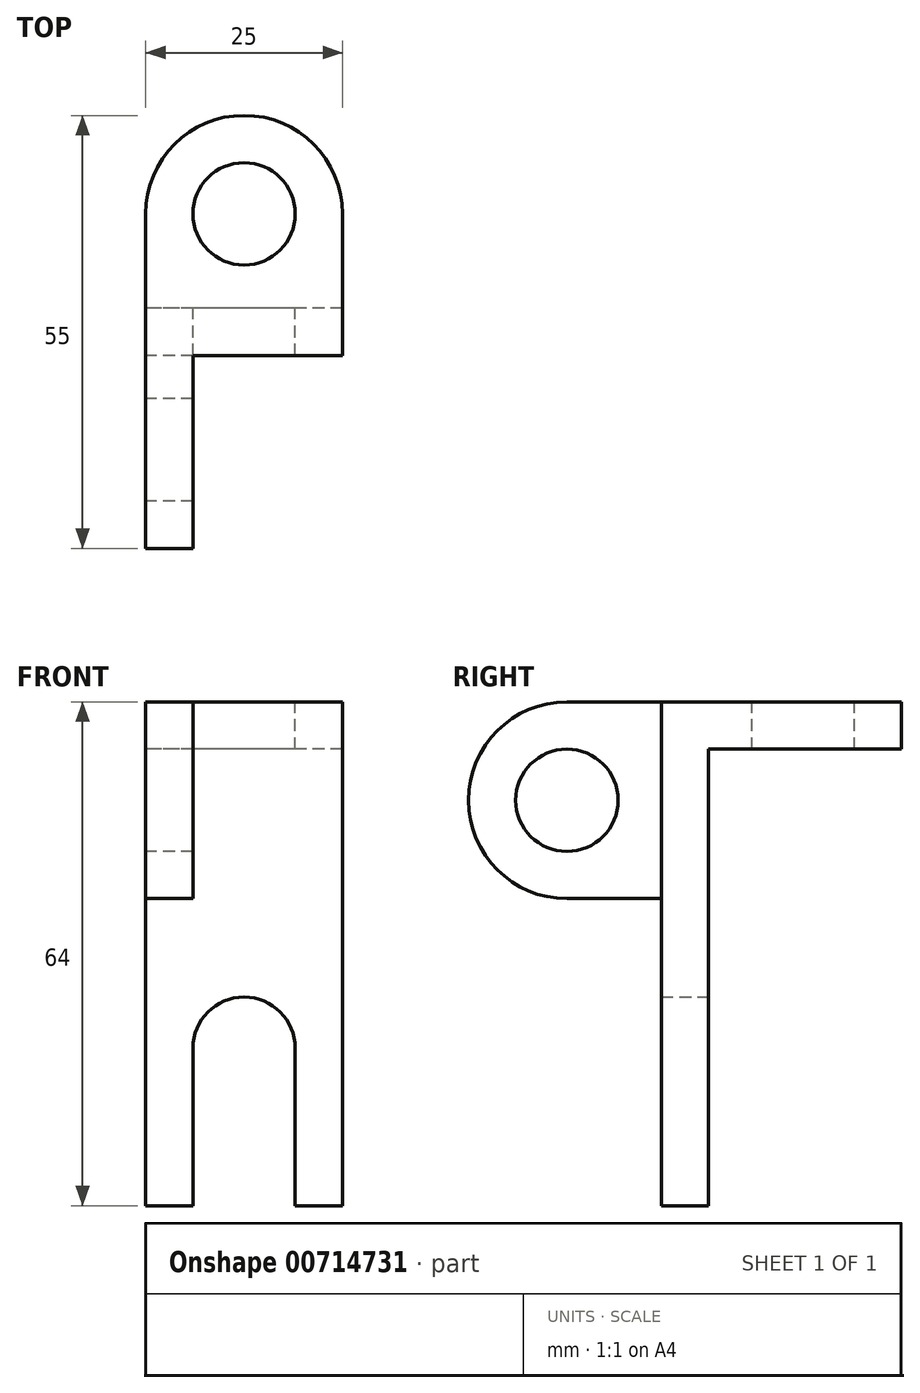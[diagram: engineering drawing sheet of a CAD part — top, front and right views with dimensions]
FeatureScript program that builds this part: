
annotation { "Feature Type Name" : "Feature", "Feature Type Description" : "" }
export const myFeature = defineFeature(function(context is Context, id is Id, definition is map)
    precondition{}
    {
        {
            var Q0;
            Q0=qCreatedBy(makeId("Front.planeOp"),FACE);
            var sketch = newSketch(context, id + "F0", { "sketchPlane" : qUnion([Q0])});
            skLineSegment(sketch, "E0.bottom", {"start": v(12.5, 32) * mm, "end": v(-12.5, 32) * mm});
            skLineSegment(sketch, "E0.top", {"start": v(12.5, -32) * mm, "end": v(-12.5, -32) * mm});
            skLineSegment(sketch, "E0.left", {"start": v(12.5, 32) * mm, "end": v(12.5, -32) * mm});
            skLineSegment(sketch, "E0.right", {"start": v(-12.5, 32) * mm, "end": v(-12.5, -32) * mm});
            skPoint(sketch, "E0.middle", {"position": v(0, 0) * mm});
            skLineSegment(sketch, "E1.bottom", {"start": v(6.5, -32) * mm, "end": v(-6.5, -32) * mm});
            skLineSegment(sketch, "E1.top", {"start": v(6.5, -12) * mm, "end": v(-6.5, -12) * mm});
            skLineSegment(sketch, "E1.left", {"start": v(6.5, -32) * mm, "end": v(6.5, -12) * mm});
            skLineSegment(sketch, "E1.right", {"start": v(-6.5, -32) * mm, "end": v(-6.5, -12) * mm});
            skPoint(sketch, "E1.middle", {"position": v(0, -22) * mm});
            skCircle(sketch, "E2", {"center": v(0, -12) * mm, "radius": 6.5 * mm});
            skSolve(sketch);
        }
        {
            var Q0;
            Q0=makeQuery(id+"F0.imprint","IMPRINT",FACE,{"disambiguationData":[TD([[makeQuery(id+"F0.imprint","IMPRINT",EDGE,{"derivedFrom":sQuery(id+"F0.wireOp",EDGE,"E0.bottom")}),1.0]])]});
            extrude(context, id + "F1", {"entities" : qUnion([Q0]), "depth" : 6 * mm, "offsetDistance" : 25 * mm});
        }
        {
            var Q0;
            Q0=makeQuery(id+"F1.opExtrude","SWEPT_FACE",FACE,{"disambiguationData":[OSD([sQuery(id+"F0.wireOp",EDGE,"E0.bottom")])]});
            var sketch = newSketch(context, id + "F2", { "sketchPlane" : qUnion([Q0])});
            skLineSegment(sketch, "E3.bottom", {"start": v(12.5, -6) * mm, "end": v(-12.5, -6) * mm});
            skLineSegment(sketch, "E3.top", {"start": v(12.5, 12) * mm, "end": v(6.5, 12) * mm, "construction": true});
            skLineSegment(sketch, "E3.left", {"start": v(12.5, -6) * mm, "end": v(12.5, 12) * mm});
            skLineSegment(sketch, "E3.right", {"start": v(-12.5, -6) * mm, "end": v(-12.5, 12) * mm});
            skCircle(sketch, "E4", {"center": v(0, 12) * mm, "radius": 12.5 * mm});
            skCircle(sketch, "E5", {"center": v(0, 12) * mm, "radius": 6.5 * mm});
            skLineSegment(sketch, "E6.trimOffspring", {"start": v(-6.5, 12) * mm, "end": v(-12.5, 12) * mm, "construction": true});
            skSolve(sketch);
        }
        {
            var Q0;
            Q0=qSketchRegion(id+"F2",true);
            extrude(context, id + "F3", {"entities" : qUnion([Q0]), "operationType" : NewBodyOperationType.ADD, "oppositeDirection" : true, "depth" : 6 * mm, "offsetDistance" : 25 * mm});
        }
        {
            var Q0;
            Q0=makeQuery(id+"F3.boolean.opBoolean","MERGE",FACE,{"derivedFrom":[makeQuery(id+"F1.opExtrude","SWEPT_FACE",FACE,{"disambiguationData":[OSD([sQuery(id+"F0.wireOp",EDGE,"E0.right")])]}),makeQuery(id+"F3.opExtrude","SWEPT_FACE",FACE,{"disambiguationData":[OSD([sQuery(id+"F2.wireOp",EDGE,"E3.right")])]})]});
            var sketch = newSketch(context, id + "F4", { "sketchPlane" : qUnion([Q0])});
            skLineSegment(sketch, "E7.bottom", {"start": v(0, 32) * mm, "end": v(18, 32) * mm});
            skLineSegment(sketch, "E7.top", {"start": v(0, 7) * mm, "end": v(18, 7) * mm});
            skLineSegment(sketch, "E7.left", {"start": v(0, 32) * mm, "end": v(0, 7) * mm});
            skLineSegment(sketch, "E7.right", {"start": v(18, 32) * mm, "end": v(18, 7) * mm});
            skArc(sketch, "E8", {"start": v(18, 7) * mm, "mid": v(30.5, 19.5) * mm, "end": v(18, 32) * mm});
            skCircle(sketch, "E9", {"center": v(18, 19.5) * mm, "radius": 6.5 * mm});
            skSolve(sketch);
        }
        {
            var Q0;
            {var subQ0=sQuery(id+"F4.wireOp",EDGE,"E8");Q0=makeQuery(id+"F4.imprint","IMPRINT",FACE,{"disambiguationData":[TD([[makeQuery(id+"F4.imprint","IMPRINT",EDGE,{"derivedFrom":subQ0}),1.0]])]});}
            var Q1;
            {var subQ3=sQuery(id+"F4.wireOp",EDGE,"E7.bottom");var subQ4=sQuery(id+"F0.wireOp",EDGE,"E0.right");var subQ8=makeQuery(id+"F1.opExtrude","CAP_EDGE",EDGE,{"disambiguationData":[OSD([subQ4])],"isStart":false});var subQ10=makeQuery(id+"F4.imprint","INTERSECT",VERTEX,{"derivedFrom":[subQ8,subQ3]});Q1=makeQuery(id+"F4.imprint","IMPRINT",FACE,{"disambiguationData":[TD([[makeQuery(id+"F4.imprint","IMPRINT",EDGE,{"disambiguationData":[TD([[subQ10,-1.0]])],"derivedFrom":subQ8}),-1.0]])]});}
            var Q2;
            {var subQ1=sQuery(id+"F4.wireOp",EDGE,"E7.right");var subQ4=sQuery(id+"F4.wireOp",EDGE,"E9");var subQ5=makeQuery(id+"F4.imprint","INTERSECT",VERTEX,{"disambiguationData":[OD(0.0)],"derivedFrom":[subQ1,subQ4]});Q2=makeQuery(id+"F4.imprint","IMPRINT",FACE,{"disambiguationData":[TD([[makeQuery(id+"F4.imprint","IMPRINT",EDGE,{"disambiguationData":[TD([[subQ5,-1.0]])],"derivedFrom":subQ4}),-1.0]])]});}
            extrude(context, id + "F5", {"entities" : qUnion([Q0, Q1, Q2]), "operationType" : NewBodyOperationType.ADD, "oppositeDirection" : true, "depth" : 6 * mm, "offsetDistance" : 25 * mm});
        }
    });
